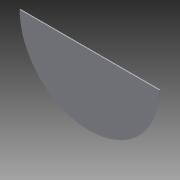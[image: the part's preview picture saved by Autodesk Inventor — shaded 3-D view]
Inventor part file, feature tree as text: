
AUTODESK INVENTOR PART (.ipt)
format: ipt  version: 2015 (Build 190159000, 159)  size: 73,728 bytes
history: native  units: mm
features: extrude x1, sketch x1
ambient origin geometry x8: Origin, YZ Plane, XZ Plane, XY Plane, X Axis, Y Axis, Z Axis, Center Point
bodies: Solid1 (feature_tree)
feature tree (2):
  extrude  "Extrusion1"  TaperAngle=180.0deg  [1 undecoded]
  sketch  "Sketch1"  dims[d0=300.0mm d1=180.0deg d2=4.0mm d3=0.0mm]
note: 1 required parameter value undecoded (feature->parameter linkage not recoverable at this tier; creation-order binding heuristic only, values carry confidence <= 0.55)
